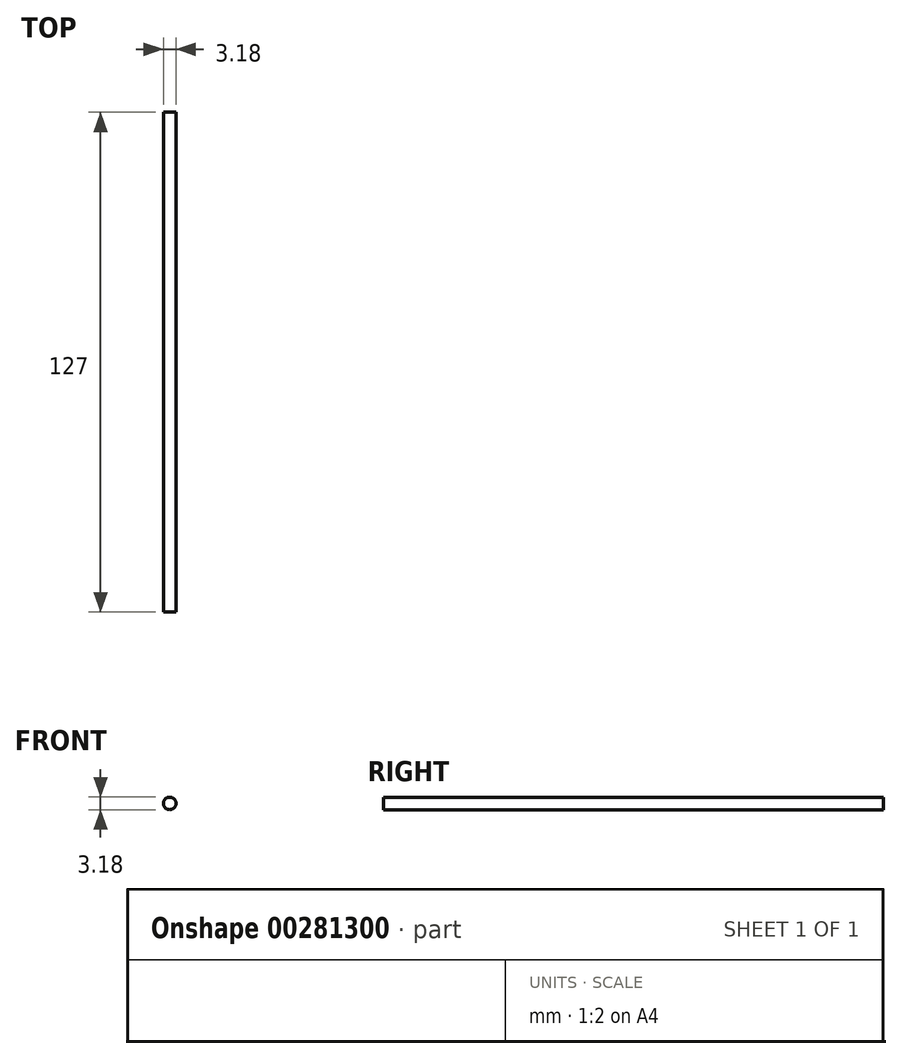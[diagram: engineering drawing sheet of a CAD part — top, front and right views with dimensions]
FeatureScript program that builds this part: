
annotation { "Feature Type Name" : "Feature", "Feature Type Description" : "" }
export const myFeature = defineFeature(function(context is Context, id is Id, definition is map)
    precondition{}
    {
        {
            var Q0;
            Q0=qCreatedBy(makeId("Front.planeOp"),FACE);
            var sketch = newSketch(context, id + "F0", { "sketchPlane" : qUnion([Q0])});
            skCircle(sketch, "E0", {"center": v(0, 0) * mm, "radius": 1.59 * mm});
            skSolve(sketch);
        }
        {
            var Q0;
            Q0 = qSketchRegion(id + "F0", true);
            extrude(context, id + "F1", {"entities" : qUnion([Q0]), "depth" : 127 * mm});
        }
    });
